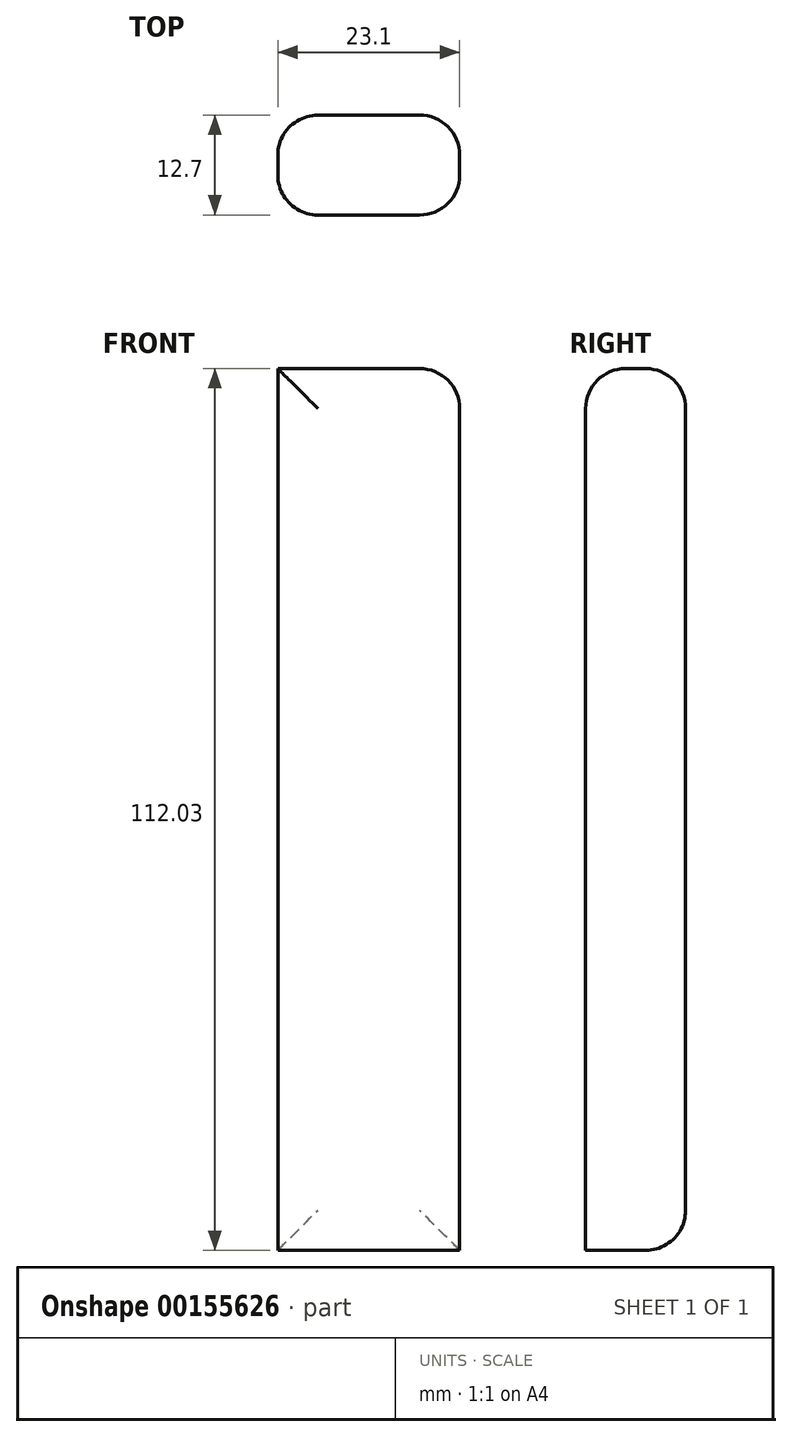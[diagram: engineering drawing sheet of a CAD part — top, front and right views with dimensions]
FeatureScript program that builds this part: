
annotation { "Feature Type Name" : "Feature", "Feature Type Description" : "" }
export const myFeature = defineFeature(function(context is Context, id is Id, definition is map)
    precondition{}
    {
        {
            var Q0;
            Q0=qCreatedBy(makeId("Front.planeOp"),FACE);
            var sketch = newSketch(context, id + "F0", { "sketchPlane" : qUnion([Q0])});
            skLineSegment(sketch, "E0", {"start": v(-41.92, 43.47) * mm, "end": v(-41.92, -68.56) * mm});
            skLineSegment(sketch, "E1", {"start": v(-41.92, -68.56) * mm, "end": v(-18.82, -68.56) * mm});
            skLineSegment(sketch, "E2", {"start": v(-18.82, -68.56) * mm, "end": v(-18.82, 43.47) * mm});
            skLineSegment(sketch, "E3", {"start": v(-18.82, 43.47) * mm, "end": v(-41.92, 43.47) * mm});
            skSolve(sketch);
        }
        {
            var Q0;
            Q0=makeQuery(id+"F0.imprint","IMPRINT",FACE,{"disambiguationData":[TD([[makeQuery(id+"F0.imprint","IMPRINT",EDGE,{"derivedFrom":sQuery(id+"F0.wireOp",EDGE,"E0")}),1.0]])]});
            extrude(context, id + "F1", {"entities" : qUnion([Q0]), "depth" : 12.7 * mm});
        }
        {
            var Q0;
            Q0=makeQuery(id+"F1.opExtrude","CAP_EDGE",EDGE,{"disambiguationData":[OSD([sQuery(id+"F0.wireOp",EDGE,"E3")])],"isStart":false});
            var Q1;
            Q1=makeQuery(id+"F1.opExtrude","CAP_EDGE",EDGE,{"disambiguationData":[OSD([sQuery(id+"F0.wireOp",EDGE,"E3")])],"isStart":true});
            var Q2;
            Q2=makeQuery(id+"F1.opExtrude","SWEPT_EDGE",EDGE,{"disambiguationData":[OSD([sQuery(id+"F0.wireOp",EDGE,"E2"),sQuery(id+"F0.wireOp",EDGE,"E3")])]});
            var Q3;
            Q3=makeQuery(id+"F1.opExtrude","CAP_EDGE",EDGE,{"disambiguationData":[OSD([sQuery(id+"F0.wireOp",EDGE,"E2")])],"isStart":false});
            var Q4;
            Q4=makeQuery(id+"F1.opExtrude","CAP_EDGE",EDGE,{"disambiguationData":[OSD([sQuery(id+"F0.wireOp",EDGE,"E0")])],"isStart":false});
            var Q5;
            Q5=makeQuery(id+"F1.opExtrude","CAP_EDGE",EDGE,{"disambiguationData":[OSD([sQuery(id+"F0.wireOp",EDGE,"E0")])],"isStart":true});
            var Q6;
            Q6=makeQuery(id+"F1.opExtrude","CAP_FACE",FACE,{"disambiguationData":[OSD([sQuery(id+"F0.wireOp",EDGE,"E0"),sQuery(id+"F0.wireOp",EDGE,"E1"),sQuery(id+"F0.wireOp",EDGE,"E2"),sQuery(id+"F0.wireOp",EDGE,"E3")])],"isStart":true});
            var Q7;
            Q7=makeQuery(id+"F1.opExtrude","CAP_EDGE",EDGE,{"disambiguationData":[OSD([sQuery(id+"F0.wireOp",EDGE,"E2")])],"isStart":true});
            fillet(context, id + "F2", {"entities" : qUnion([Q0, Q1, Q2, Q3, Q4, Q5, Q6, Q7]), "radius" : 5.08 * mm, "tangentPropagation" : true, "allowEdgeOverflow" : false});
        }
    });
